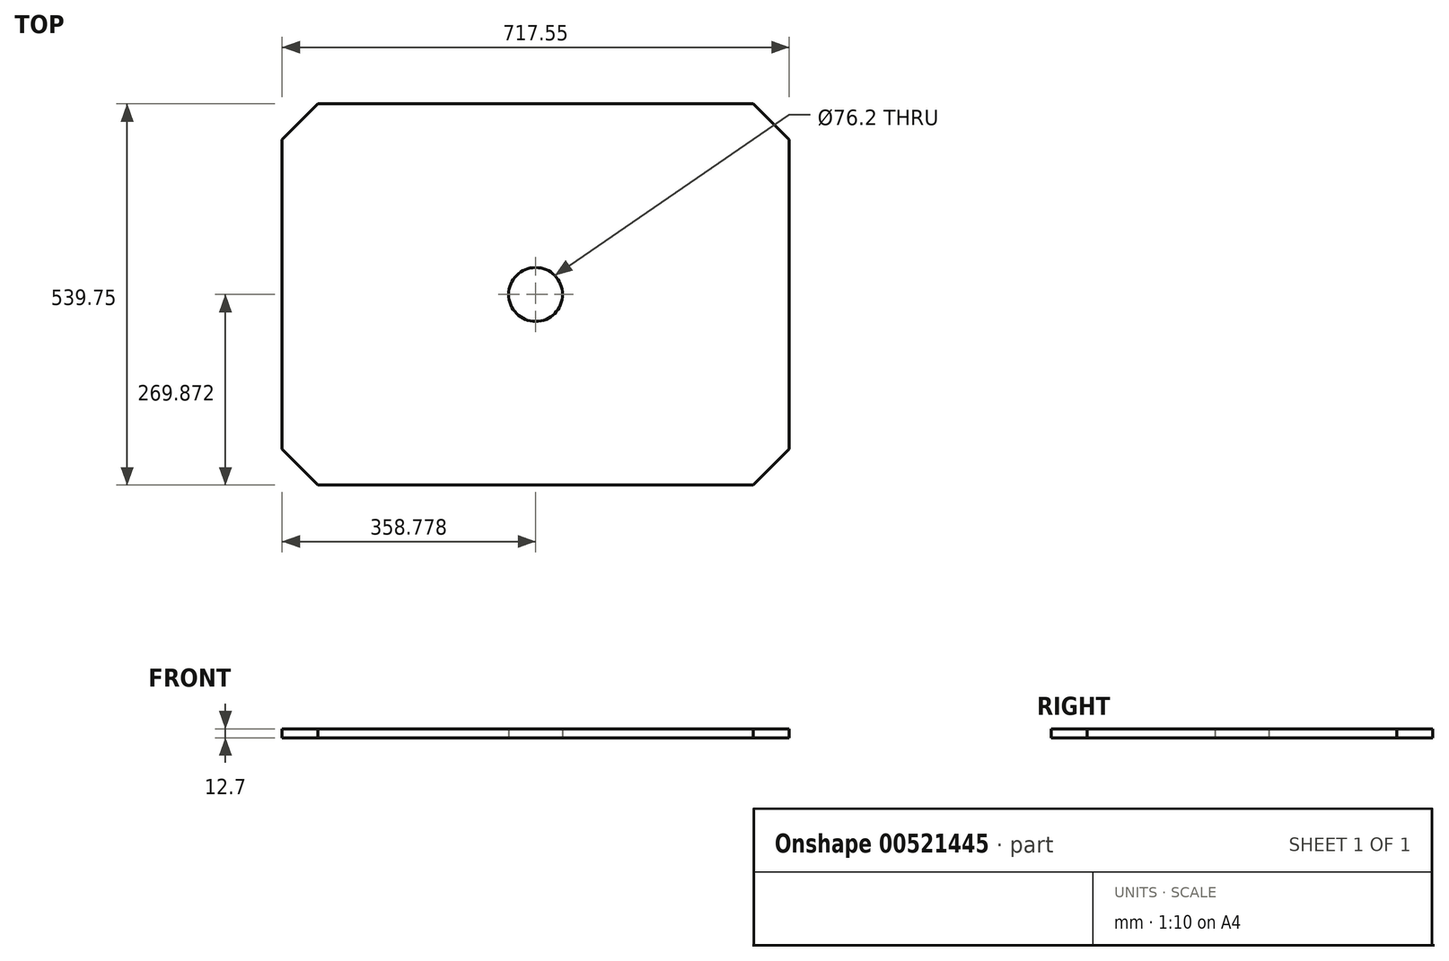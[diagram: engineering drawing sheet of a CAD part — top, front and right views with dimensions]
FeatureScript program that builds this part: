
annotation { "Feature Type Name" : "Feature", "Feature Type Description" : "" }
export const myFeature = defineFeature(function(context is Context, id is Id, definition is map)
    precondition{}
    {
        {
            var Q0;
            Q0=qCreatedBy(makeId("Top.planeOp"),FACE);
            var sketch = newSketch(context, id + "F0", { "sketchPlane" : qUnion([Q0])});
            skLineSegment(sketch, "E0.bottom", {"start": v(-267.44, 384.19) * mm, "end": v(450.11, 384.19) * mm});
            skLineSegment(sketch, "E0.top", {"start": v(-267.44, -155.56) * mm, "end": v(450.11, -155.56) * mm});
            skLineSegment(sketch, "E0.left", {"start": v(-267.44, 384.19) * mm, "end": v(-267.44, -155.56) * mm});
            skLineSegment(sketch, "E0.right", {"start": v(450.11, 384.19) * mm, "end": v(450.11, -155.56) * mm});
            skSolve(sketch);
        }
        {
            var Q0;
            Q0=makeQuery(id+"F0.imprint","IMPRINT",FACE,{"disambiguationData":[TD([[makeQuery(id+"F0.imprint","IMPRINT",EDGE,{"derivedFrom":sQuery(id+"F0.wireOp",EDGE,"E0.bottom")}),-1.0]])]});
            extrude(context, id + "F1", {"entities" : qUnion([Q0]), "depth" : 12.7 * mm, "offsetDistance" : 25.4 * mm});
        }
        {
            var Q0;
            Q0=makeQuery(id+"F1.opExtrude","SWEPT_EDGE",EDGE,{"disambiguationData":[OSD([sQuery(id+"F0.wireOp",EDGE,"E0.bottom"),sQuery(id+"F0.wireOp",EDGE,"E0.right")])]});
            var Q1;
            Q1=makeQuery(id+"F1.opExtrude","SWEPT_EDGE",EDGE,{"disambiguationData":[OSD([sQuery(id+"F0.wireOp",EDGE,"E0.top"),sQuery(id+"F0.wireOp",EDGE,"E0.right")])]});
            var Q2;
            Q2=makeQuery(id+"F1.opExtrude","SWEPT_EDGE",EDGE,{"disambiguationData":[OSD([sQuery(id+"F0.wireOp",EDGE,"E0.top"),sQuery(id+"F0.wireOp",EDGE,"E0.left")])]});
            var Q3;
            Q3=makeQuery(id+"F1.opExtrude","SWEPT_EDGE",EDGE,{"disambiguationData":[OSD([sQuery(id+"F0.wireOp",EDGE,"E0.bottom"),sQuery(id+"F0.wireOp",EDGE,"E0.left")])]});
            chamfer(context, id + "F2", {"entities" : qUnion([Q0, Q1, Q2, Q3]), "width" : 50.8 * mm, "tangentPropagation" : true});
        }
        {
            var Q0;
            Q0=makeQuery(id+"F1.opExtrude","CAP_FACE",FACE,{"disambiguationData":[OSD([sQuery(id+"F0.wireOp",EDGE,"E0.bottom"),sQuery(id+"F0.wireOp",EDGE,"E0.top"),sQuery(id+"F0.wireOp",EDGE,"E0.left"),sQuery(id+"F0.wireOp",EDGE,"E0.right")])],"isStart":true});
            var sketch = newSketch(context, id + "F3", { "sketchPlane" : qUnion([Q0])});
            skLineSegment(sketch, "E1", {"start": v(91.34, 155.56) * mm, "end": v(91.34, -384.19) * mm});
            skPoint(sketch, "E2", {"position": v(91.34, -114.31) * mm});
            skSolve(sketch);
        }
        {
            var Q0;
            Q0=sQuery(id+"F3.wireOp",VERTEX,"E2");
            var Q1;
            Q1=makeQuery(id+"F1.opExtrude","SWEPT_BODY",BODY,{"disambiguationData":[OSD([sQuery(id+"F0.wireOp",EDGE,"E0.bottom"),sQuery(id+"F0.wireOp",EDGE,"E0.top"),sQuery(id+"F0.wireOp",EDGE,"E0.left"),sQuery(id+"F0.wireOp",EDGE,"E0.right")])]});
            hole(context, id + "F4", {"style" : HoleStyle.SIMPLE, "endStyle" : HoleEndStyle.THROUGH, "holeDiameter" : 76.2 * mm, "isTappedThrough" : true, "tappedDepth" : 12.7 * mm, "tapClearance" : 3, "locations" : qUnion([Q0]), "scope" : qUnion([Q1])});
        }
    });
